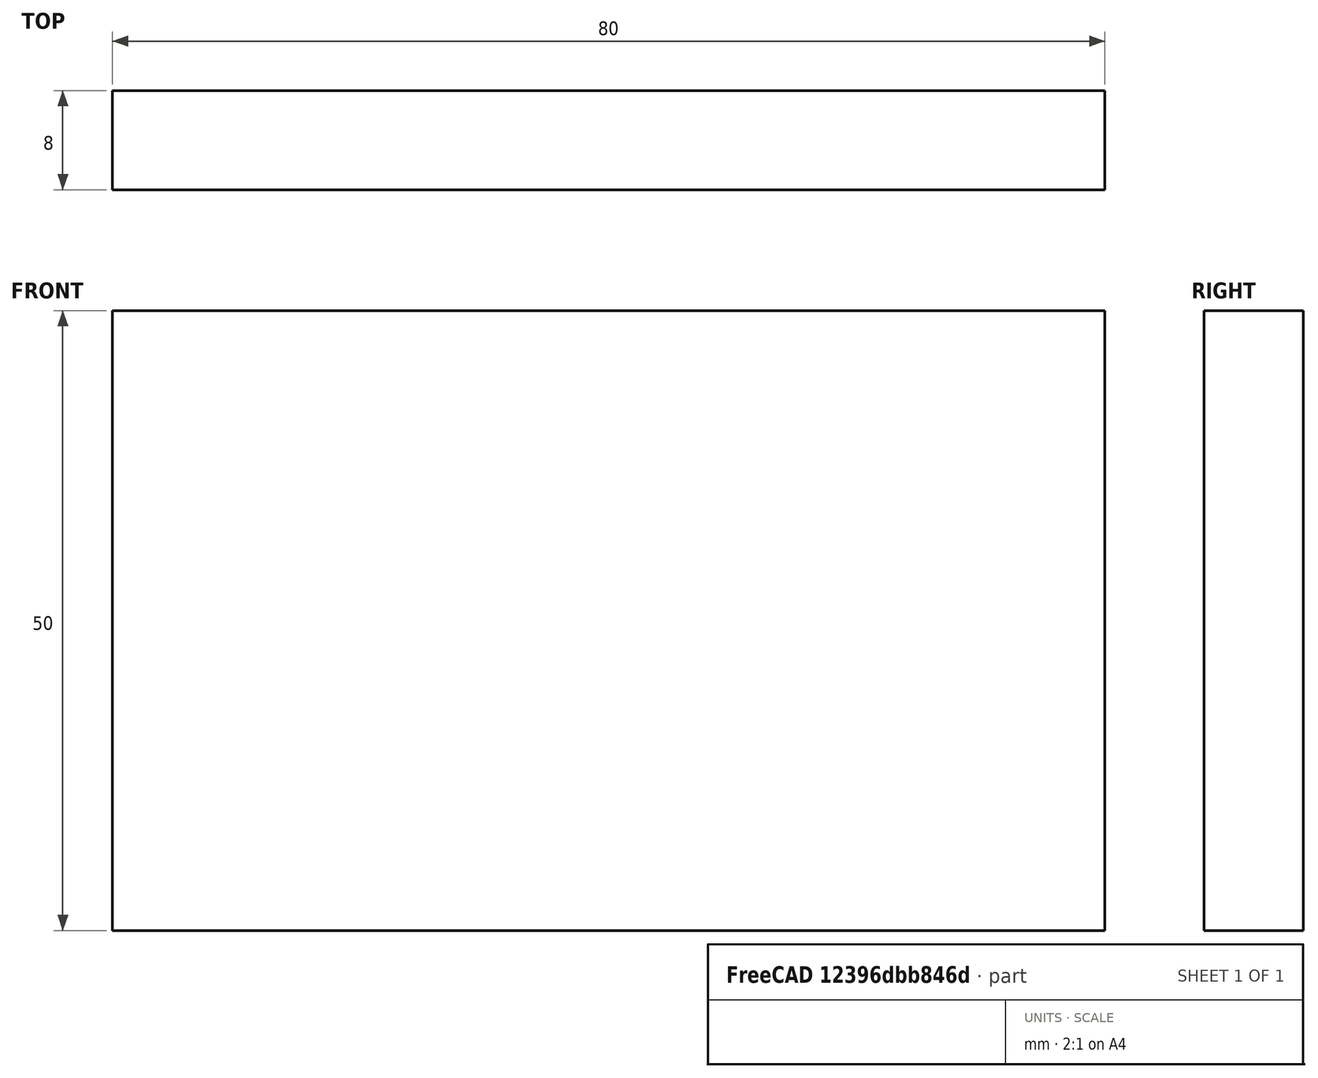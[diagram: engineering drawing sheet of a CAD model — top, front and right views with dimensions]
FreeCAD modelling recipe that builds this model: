
FCSTD DOCUMENT  (FreeCAD 0.15R4671 (Git))
Label: Flat Bar 80x8 EN10058 S235JR
License: All rights reserved
LicenseURL: http://en.wikipedia.org/wiki/All_rights_reserved
objects: Sketcher::SketchObject×1, Part::Extrusion×1
note: 2 computed .brp shape members not serialized (recipe doc carries the construction recipe); baked Part::Feature solids carry a one-line shape summary decoded from their .brp

FEATURE [Sketcher::SketchObject] Sketch
  sketch-geometry (4):
    g0: LineSegment StartX=-40 StartY=-4 StartZ=0 EndX=40 EndY=-4 EndZ=0
    g1: LineSegment StartX=40 StartY=-4 StartZ=0 EndX=40 EndY=4 EndZ=0
    g2: LineSegment StartX=40 StartY=4 StartZ=0 EndX=-40 EndY=4 EndZ=0
    g3: LineSegment StartX=-40 StartY=4 StartZ=0 EndX=-40 EndY=-4 EndZ=0
  constraints (12):
    c: Coincident(g0,g1)
    c: Coincident(g1,g2)
    c: Coincident(g2,g3)
    c: Coincident(g3,g0)
    c: Horizontal(g0)
    c: Horizontal(g2)
    c: Vertical(g1)
    c: Vertical(g3)
    c: Symmetric(g1,g2,g-2)
    c: Symmetric(g0,g1,g-1)
    c: DistanceY(g1) = 8
    c: DistanceX(g0) = 80
FEATURE [Part::Extrusion] Extrude  label="Flat Bar 80x8 EN10058 S235JR"
  Base = -> Sketch
  Dir = (0,0,50)
  Solid = true
